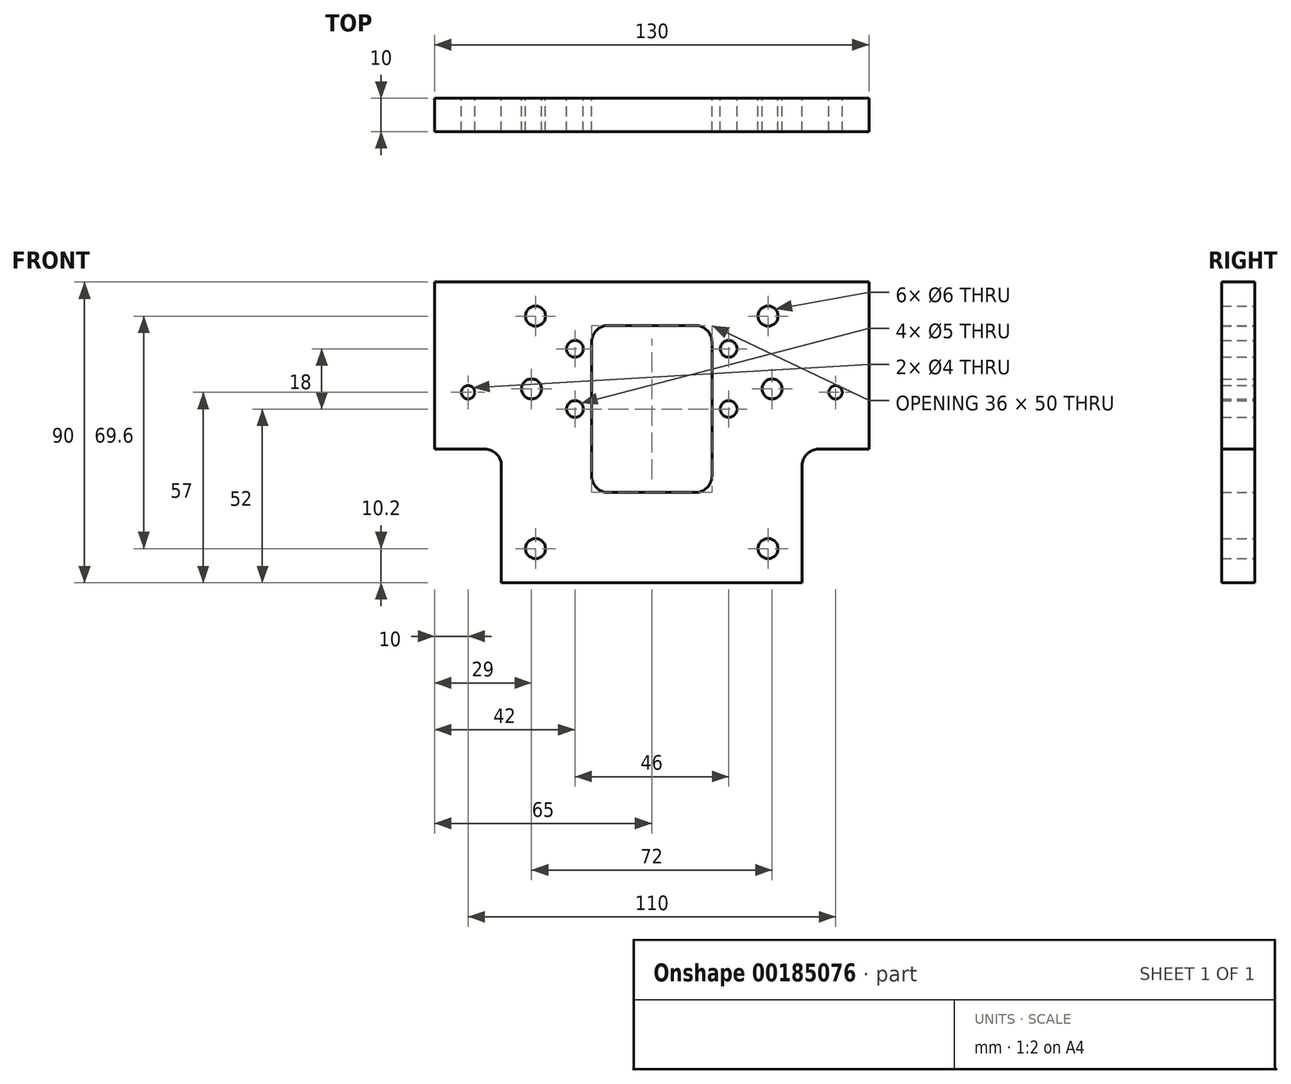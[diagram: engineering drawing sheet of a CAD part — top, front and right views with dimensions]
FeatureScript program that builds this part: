
annotation { "Feature Type Name" : "Feature", "Feature Type Description" : "" }
export const myFeature = defineFeature(function(context is Context, id is Id, definition is map)
    precondition{}
    {
        {
            var Q0;
            Q0=qCreatedBy(makeId("Front.planeOp"),FACE);
            var sketch = newSketch(context, id + "F0", { "sketchPlane" : qUnion([Q0])});
            skCircle(sketch, "E0", {"center": v(-36, 0) * mm, "radius": 3 * mm});
            skCircle(sketch, "E1", {"center": v(36, 0) * mm, "radius": 3 * mm});
            skCircle(sketch, "E2", {"center": v(-55, -1) * mm, "radius": 2 * mm});
            skCircle(sketch, "E3", {"center": v(55, -1) * mm, "radius": 2 * mm});
            skLineSegment(sketch, "E4.bottom", {"start": v(13, 19) * mm, "end": v(-13, 19) * mm});
            skLineSegment(sketch, "E4.top", {"start": v(13, -31) * mm, "end": v(-13, -31) * mm});
            skLineSegment(sketch, "E4.left", {"start": v(18, 14) * mm, "end": v(18, -26) * mm});
            skLineSegment(sketch, "E4.right", {"start": v(-18, 14) * mm, "end": v(-18, -26) * mm});
            skPoint(sketch, "E4.middle", {"position": v(0, -6) * mm});
            skPoint(sketch, "E5.visualSharp", {"position": v(-18, 19) * mm});
            skArc(sketch, "E5.filletArc", {"start": v(-13, 19) * mm, "mid": v(-16.54, 17.54) * mm, "end": v(-18, 14) * mm});
            skPoint(sketch, "E6.visualSharp", {"position": v(18, 19) * mm});
            skArc(sketch, "E6.filletArc", {"start": v(18, 14) * mm, "mid": v(16.54, 17.54) * mm, "end": v(13, 19) * mm});
            skPoint(sketch, "E7.visualSharp", {"position": v(18, -31) * mm});
            skArc(sketch, "E7.filletArc", {"start": v(13, -31) * mm, "mid": v(16.54, -29.54) * mm, "end": v(18, -26) * mm});
            skPoint(sketch, "E8.visualSharp", {"position": v(-18, -31) * mm});
            skArc(sketch, "E8.filletArc", {"start": v(-18, -26) * mm, "mid": v(-16.54, -29.54) * mm, "end": v(-13, -31) * mm});
            skSolve(sketch);
        }
        {
            var Q0;
            Q0=qCreatedBy(makeId("Front.planeOp"),FACE);
            var sketch = newSketch(context, id + "F1", { "sketchPlane" : qUnion([Q0])});
            skLineSegment(sketch, "E9.bottom", {"start": v(-65, -58) * mm, "end": v(65, -58) * mm});
            skLineSegment(sketch, "E9.top", {"start": v(-65, 32) * mm, "end": v(65, 32) * mm});
            skLineSegment(sketch, "E9.left", {"start": v(-65, -58) * mm, "end": v(-65, 32) * mm});
            skLineSegment(sketch, "E9.right", {"start": v(65, -58) * mm, "end": v(65, 32) * mm});
            skSolve(sketch);
        }
        {
            var Q0;
            Q0=qCreatedBy(makeId("Front.planeOp"),FACE);
            var sketch = newSketch(context, id + "F2", { "sketchPlane" : qUnion([Q0])});
            skCircle(sketch, "E10", {"center": v(23, -6) * mm, "radius": 2.5 * mm});
            skCircle(sketch, "E11", {"center": v(23, 12) * mm, "radius": 2.5 * mm});
            skCircle(sketch, "E12.MirrorC", {"center": v(-23, -6) * mm, "radius": 2.5 * mm});
            skCircle(sketch, "E13.MirrorC", {"center": v(-23, 12) * mm, "radius": 2.5 * mm});
            skSolve(sketch);
        }
        {
            var Q0;
            Q0 = qSketchRegion(id + "F1", true);
            extrude(context, id + "F3", {"entities" : qUnion([Q0]), "depth" : 10 * mm});
        }
        {
            var Q0;
            Q0 = qSketchRegion(id + "F2", true);
            extrude(context, id + "F4", {"entities" : qUnion([Q0]), "operationType" : NewBodyOperationType.REMOVE, "endBound" : BoundingType.THROUGH_ALL, "depth" : 25 * mm});
        }
        {
            var Q0;
            Q0 = qSketchRegion(id + "F0", true);
            extrude(context, id + "F5", {"entities" : qUnion([Q0]), "operationType" : NewBodyOperationType.REMOVE, "endBound" : BoundingType.THROUGH_ALL, "depth" : 25 * mm});
        }
        {
            var Q0;
            Q0=qCreatedBy(makeId("Front.planeOp"),FACE);
            var sketch = newSketch(context, id + "F6", { "sketchPlane" : qUnion([Q0])});
            skCircle(sketch, "E14", {"center": v(34.8, -47.8) * mm, "radius": 3 * mm});
            skCircle(sketch, "E15", {"center": v(34.8, 21.8) * mm, "radius": 3 * mm});
            skCircle(sketch, "E16.MirrorC", {"center": v(-34.8, -47.8) * mm, "radius": 3 * mm});
            skCircle(sketch, "E17.MirrorC", {"center": v(-34.8, 21.8) * mm, "radius": 3 * mm});
            skSolve(sketch);
        }
        {
            var Q0;
            Q0 = qSketchRegion(id + "F6", true);
            extrude(context, id + "F7", {"entities" : qUnion([Q0]), "operationType" : NewBodyOperationType.REMOVE, "endBound" : BoundingType.THROUGH_ALL, "depth" : 25 * mm});
        }
        {
            var Q0;
            Q0=qCreatedBy(makeId("Front.planeOp"),FACE);
            var sketch = newSketch(context, id + "F8", { "sketchPlane" : qUnion([Q0])});
            skLineSegment(sketch, "E18.bottom", {"start": v(-65, -58) * mm, "end": v(-45, -58) * mm});
            skLineSegment(sketch, "E18.top", {"start": v(-65, -18) * mm, "end": v(-50, -18) * mm});
            skLineSegment(sketch, "E18.left", {"start": v(-65, -58) * mm, "end": v(-65, -18) * mm});
            skLineSegment(sketch, "E18.right", {"start": v(-45, -58) * mm, "end": v(-45, -23) * mm});
            skPoint(sketch, "E19.visualSharp", {"position": v(-45, -18) * mm});
            skArc(sketch, "E19.filletArc", {"start": v(-45, -23) * mm, "mid": v(-46.46, -19.46) * mm, "end": v(-50, -18) * mm});
            skPoint(sketch, "E20.MirrorP", {"position": v(45, -18) * mm});
            skLineSegment(sketch, "E21.MirrorCS", {"start": v(65, -58) * mm, "end": v(45, -58) * mm});
            skLineSegment(sketch, "E22.MirrorCS", {"start": v(65, -18) * mm, "end": v(50, -18) * mm});
            skLineSegment(sketch, "E23.MirrorCS", {"start": v(45, -58) * mm, "end": v(45, -23) * mm});
            skLineSegment(sketch, "E24.MirrorCS", {"start": v(65, -58) * mm, "end": v(65, -18) * mm});
            skArc(sketch, "E25.MirrorCS", {"start": v(45, -23) * mm, "mid": v(46.46, -19.46) * mm, "end": v(50, -18) * mm});
            skSolve(sketch);
        }
        {
            var Q0;
            Q0 = qSketchRegion(id + "F8", true);
            extrude(context, id + "F9", {"entities" : qUnion([Q0]), "operationType" : NewBodyOperationType.REMOVE, "endBound" : BoundingType.THROUGH_ALL, "depth" : 25 * mm});
        }
    });
